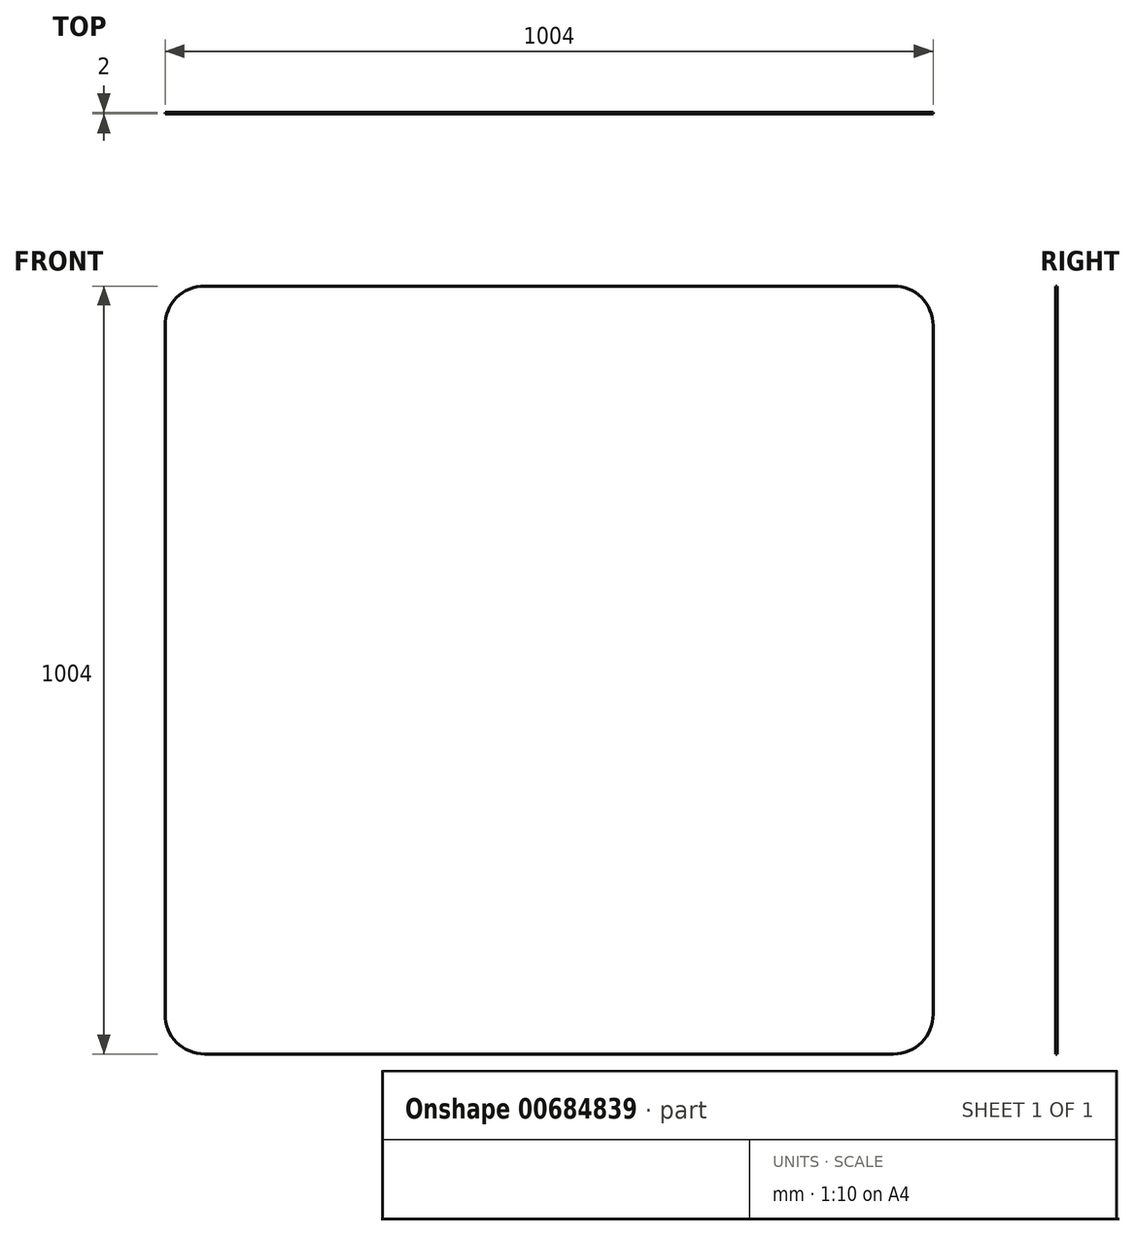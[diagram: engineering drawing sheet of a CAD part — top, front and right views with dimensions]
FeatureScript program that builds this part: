
annotation { "Feature Type Name" : "Feature", "Feature Type Description" : "" }
export const myFeature = defineFeature(function(context is Context, id is Id, definition is map)
    precondition{}
    {
        {
            var Q0;
            Q0=qCreatedBy(makeId("Front.planeOp"),FACE);
            var sketch = newSketch(context, id + "F0", { "sketchPlane" : qUnion([Q0])});
            skLineSegment(sketch, "E0.bottom", {"start": v(-450, 500) * mm, "end": v(450, 500) * mm});
            skLineSegment(sketch, "E0.top", {"start": v(-450, -500) * mm, "end": v(450, -500) * mm});
            skLineSegment(sketch, "E0.left", {"start": v(-500, 450) * mm, "end": v(-500, -450) * mm});
            skLineSegment(sketch, "E0.right", {"start": v(500, 450) * mm, "end": v(500, -450) * mm});
            skPoint(sketch, "E1.visualSharp", {"position": v(-500, -500) * mm});
            skArc(sketch, "E1.filletArc", {"start": v(-500, -450) * mm, "mid": v(-485.36, -485.36) * mm, "end": v(-450, -500) * mm});
            skPoint(sketch, "E2.visualSharp", {"position": v(500, -500) * mm});
            skArc(sketch, "E2.filletArc", {"start": v(450, -500) * mm, "mid": v(485.36, -485.36) * mm, "end": v(500, -450) * mm});
            skPoint(sketch, "E3.visualSharp", {"position": v(-500, 500) * mm});
            skArc(sketch, "E3.filletArc", {"start": v(-450, 500) * mm, "mid": v(-485.36, 485.36) * mm, "end": v(-500, 450) * mm});
            skPoint(sketch, "E4.visualSharp", {"position": v(500, 500) * mm});
            skArc(sketch, "E4.filletArc", {"start": v(500, 450) * mm, "mid": v(485.36, 485.36) * mm, "end": v(450, 500) * mm});
            skArc(sketch, "E5.0", {"start": v(-502, -450) * mm, "mid": v(-486.77, -486.77) * mm, "end": v(-450, -502) * mm});
            skLineSegment(sketch, "E5.1", {"start": v(-502, 450) * mm, "end": v(-502, -450) * mm});
            skLineSegment(sketch, "E5.2", {"start": v(-450, -502) * mm, "end": v(450, -502) * mm});
            skArc(sketch, "E5.3", {"start": v(-450, 502) * mm, "mid": v(-486.77, 486.77) * mm, "end": v(-502, 450) * mm});
            skArc(sketch, "E5.4", {"start": v(450, -502) * mm, "mid": v(486.77, -486.77) * mm, "end": v(502, -450) * mm});
            skLineSegment(sketch, "E5.5", {"start": v(502, 450) * mm, "end": v(502, -450) * mm});
            skArc(sketch, "E5.6", {"start": v(502, 450) * mm, "mid": v(486.77, 486.77) * mm, "end": v(450, 502) * mm});
            skLineSegment(sketch, "E5.7", {"start": v(-450, 502) * mm, "end": v(450, 502) * mm});
            skSolve(sketch);
        }
        {
            var Q0;
            Q0=makeQuery(id+"F0.imprint","IMPRINT",FACE,{"disambiguationData":[TD([[makeQuery(id+"F0.imprint","IMPRINT",EDGE,{"derivedFrom":sQuery(id+"F0.wireOp",EDGE,"E0.bottom")}),-1.0]])]});
            var Q1;
            Q1=makeQuery(id+"F0.imprint","IMPRINT",FACE,{"disambiguationData":[TD([[makeQuery(id+"F0.imprint","IMPRINT",EDGE,{"derivedFrom":sQuery(id+"F0.wireOp",EDGE,"E0.bottom")}),1.0]])]});
            extrude(context, id + "F1", {"entities" : qUnion([Q0, Q1]), "depth" : 2 * mm, "offsetDistance" : 25 * mm});
        }
    });
